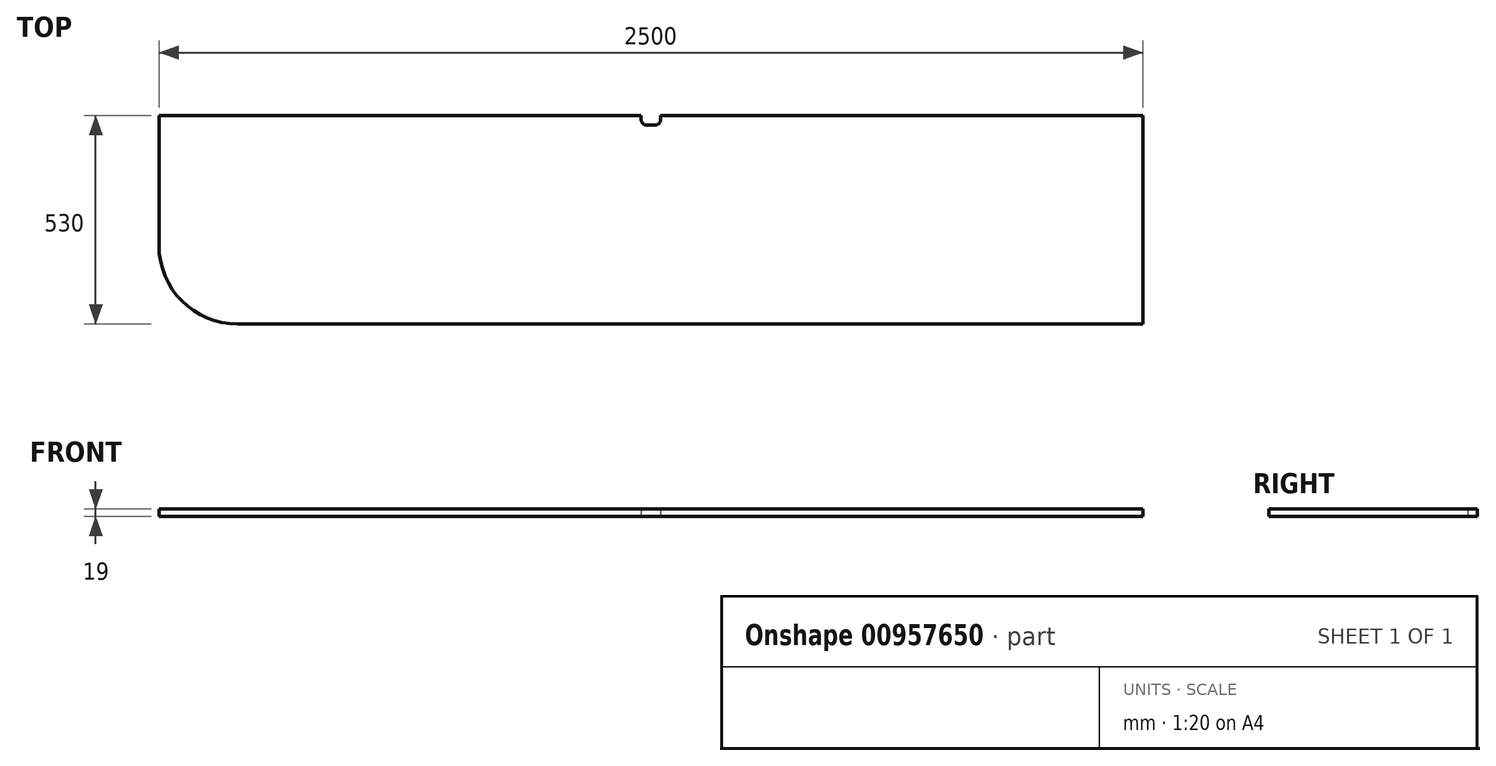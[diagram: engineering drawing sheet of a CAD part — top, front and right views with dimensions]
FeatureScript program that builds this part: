
annotation { "Feature Type Name" : "Feature", "Feature Type Description" : "" }
export const myFeature = defineFeature(function(context is Context, id is Id, definition is map)
    precondition{}
    {
        {
            var Q0;
            Q0=qCreatedBy(makeId("Top.planeOp"),FACE);
            var sketch = newSketch(context, id + "F0", { "sketchPlane" : qUnion([Q0])});
            skLineSegment(sketch, "E0.bottom", {"start": v(-1250, 265) * mm, "end": v(-25, 265) * mm});
            skLineSegment(sketch, "E0.top", {"start": v(-1050, -265) * mm, "end": v(1250, -265) * mm});
            skLineSegment(sketch, "E0.left", {"start": v(-1250, 265) * mm, "end": v(-1250, -65) * mm});
            skLineSegment(sketch, "E0.right", {"start": v(1250, 265) * mm, "end": v(1250, -265) * mm});
            skPoint(sketch, "E0.middle", {"position": v(0, 0) * mm});
            skPoint(sketch, "E1.visualSharp", {"position": v(-1250, -265) * mm});
            skArc(sketch, "E1.filletArc", {"start": v(-1250, -65) * mm, "mid": v(-1191.42, -206.42) * mm, "end": v(-1050, -265) * mm});
            skLineSegment(sketch, "E2.bottom", {"start": v(10, 240) * mm, "end": v(-10, 240) * mm});
            skLineSegment(sketch, "E2.left", {"start": v(25, 255) * mm, "end": v(25, 265) * mm});
            skLineSegment(sketch, "E2.right", {"start": v(-25, 255) * mm, "end": v(-25, 265) * mm});
            skPoint(sketch, "E2.middle", {"position": v(0, 265) * mm});
            skPoint(sketch, "E3.visualSharp", {"position": v(-25, 240) * mm});
            skArc(sketch, "E3.filletArc", {"start": v(-25, 255) * mm, "mid": v(-20.6, 244.4) * mm, "end": v(-10, 240) * mm});
            skPoint(sketch, "E4.visualSharp", {"position": v(25, 240) * mm});
            skArc(sketch, "E4.filletArc", {"start": v(10, 240) * mm, "mid": v(20.6, 244.4) * mm, "end": v(25, 255) * mm});
            skLineSegment(sketch, "E5.trimOffspring", {"start": v(25, 265) * mm, "end": v(1250, 265) * mm});
            skSolve(sketch);
        }
        {
            var Q0;
            Q0 = qSketchRegion(id + "F0", true);
            extrude(context, id + "F1", {"entities" : qUnion([Q0]), "depth" : 19 * mm, "offsetDistance" : 25 * mm});
        }
    });
